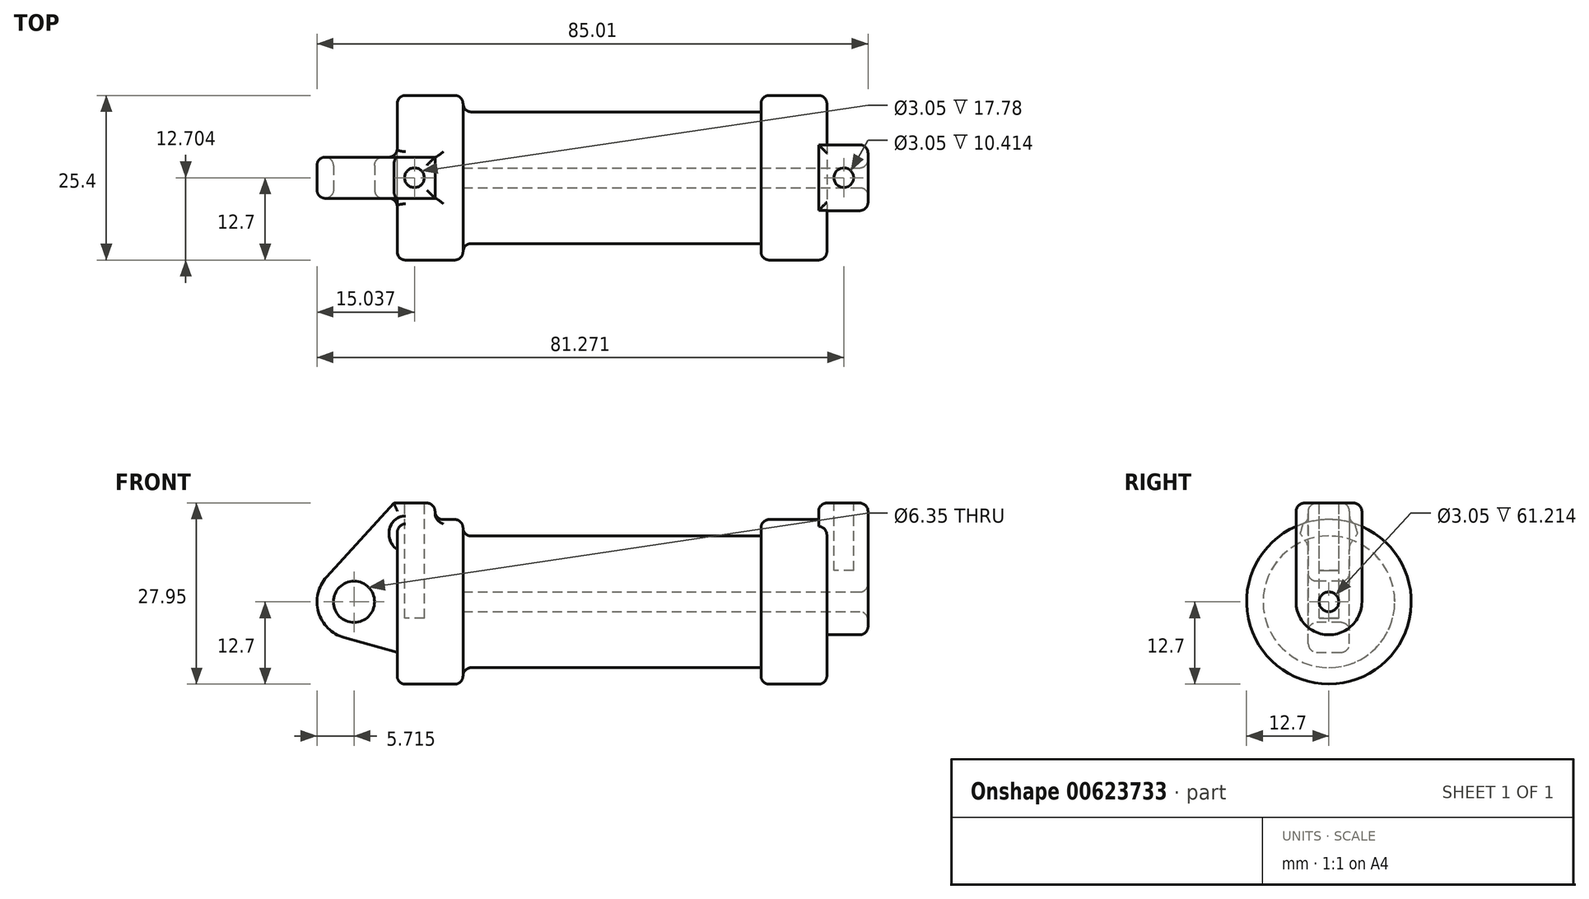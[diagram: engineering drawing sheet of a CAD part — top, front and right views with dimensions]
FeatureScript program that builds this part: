
annotation { "Feature Type Name" : "Feature", "Feature Type Description" : "" }
export const myFeature = defineFeature(function(context is Context, id is Id, definition is map)
    precondition{}
    {
        {
            var Q0;
            Q0=qCreatedBy(makeId("Front.planeOp"),FACE);
            var sketch = newSketch(context, id + "F0", { "sketchPlane" : qUnion([Q0])});
            skLineSegment(sketch, "E0", {"start": v(0, 0) * mm, "end": v(0, 12.7) * mm});
            skLineSegment(sketch, "E1", {"start": v(0, 12.7) * mm, "end": v(10.16, 12.7) * mm});
            skLineSegment(sketch, "E2", {"start": v(10.16, 12.7) * mm, "end": v(10.16, 10.16) * mm});
            skLineSegment(sketch, "E3", {"start": v(10.16, 10.16) * mm, "end": v(56.13, 10.16) * mm});
            skLineSegment(sketch, "E4", {"start": v(56.13, 10.16) * mm, "end": v(56.13, 12.7) * mm});
            skLineSegment(sketch, "E5", {"start": v(56.13, 12.7) * mm, "end": v(66.3, 12.7) * mm});
            skLineSegment(sketch, "E6", {"start": v(66.3, 12.7) * mm, "end": v(66.3, 0) * mm});
            skLineSegment(sketch, "E7", {"start": v(66.3, 0) * mm, "end": v(0, 0) * mm});
            skLineSegment(sketch, "E8", {"start": v(5.84, 15.24) * mm, "end": v(-0.5, 15.24) * mm});
            skLineSegment(sketch, "E9", {"start": v(-0.5, 15.24) * mm, "end": v(-10.88, 3.85) * mm});
            skLineSegment(sketch, "E10", {"start": v(0, 0) * mm, "end": v(-6.65, 0) * mm});
            skCircle(sketch, "E11", {"center": v(-6.65, 0) * mm, "radius": 5.72 * mm});
            skCircle(sketch, "E12", {"center": v(-6.65, 0) * mm, "radius": 3.18 * mm});
            skLineSegment(sketch, "E13", {"start": v(5.84, 15.24) * mm, "end": v(5.84, -9.4) * mm});
            skLineSegment(sketch, "E14", {"start": v(5.84, -9.4) * mm, "end": v(-8.18, -5.5) * mm});
            skSolve(sketch);
        }
        {
            var Q0;
            {var subQ0=sQuery(id+"F0.wireOp",EDGE,"E0");Q0=makeQuery(id+"F0.imprint","IMPRINT",FACE,{"disambiguationData":[TD([[makeQuery(id+"F0.imprint","IMPRINT",EDGE,{"derivedFrom":subQ0}),-1.0]])]});}
            var Q1;
            {var subQ1=sQuery(id+"F0.wireOp",EDGE,"E0");Q1=makeQuery(id+"F0.imprint","IMPRINT",FACE,{"disambiguationData":[TD([[makeQuery(id+"F0.imprint","IMPRINT",EDGE,{"derivedFrom":subQ1}),1.0]])]});}
            var Q2;
            {var subQ0=sQuery(id+"F0.wireOp",EDGE,"E14");Q2=makeQuery(id+"F0.imprint","IMPRINT",FACE,{"disambiguationData":[TD([[makeQuery(id+"F0.imprint","IMPRINT",EDGE,{"derivedFrom":subQ0}),-1.0]])]});}
            var Q3;
            {var subQ5=sQuery(id+"F0.wireOp",EDGE,"E12");Q3=makeQuery(id+"F0.imprint","IMPRINT",FACE,{"disambiguationData":[TD([[makeQuery(id+"F0.imprint","IMPRINT",EDGE,{"derivedFrom":subQ5}),-1.0]])]});}
            extrude(context, id + "F1", {"entities" : qUnion([Q0, Q1, Q2, Q3]), "endBound" : BoundingType.SYMMETRIC, "oppositeDirection" : true, "depth" : 6.35 * mm, "offsetDistance" : 25.4 * mm});
        }
        {
            var Q0;
            {var subQ0=sQuery(id+"F0.wireOp",EDGE,"E2");Q0=makeQuery(id+"F0.imprint","IMPRINT",FACE,{"disambiguationData":[TD([[makeQuery(id+"F0.imprint","IMPRINT",EDGE,{"derivedFrom":subQ0}),-1.0]])]});}
            var Q1;
            {var subQ0=sQuery(id+"F0.wireOp",EDGE,"E0");Q1=makeQuery(id+"F0.imprint","IMPRINT",FACE,{"disambiguationData":[TD([[makeQuery(id+"F0.imprint","IMPRINT",EDGE,{"derivedFrom":subQ0}),-1.0]])]});}
            var Q2;
            Q2=sQuery(id+"F0.wireOp",EDGE,"E7");
            revolve(context, id + "F2", {"operationType" : NewBodyOperationType.ADD, "entities" : qUnion([Q0, Q1]), "axis" : qUnion([Q2]), "revolveType" : RevolveType.FULL});
        }
        {
            var Q0;
            Q0=makeQuery(id+"F2.opRevolve","SWEPT_FACE",FACE,{"disambiguationData":[OSD([sQuery(id+"F0.wireOp",EDGE,"E6")])]});
            var sketch = newSketch(context, id + "F3", { "sketchPlane" : qUnion([Q0])});
            skCircle(sketch, "E15", {"center": v(0, 0) * mm, "radius": 5.08 * mm});
            skCircle(sketch, "E16", {"center": v(0, 0) * mm, "radius": 1.52 * mm});
            skLineSegment(sketch, "E17", {"start": v(5.08, 0) * mm, "end": v(5.08, 15.23) * mm});
            skLineSegment(sketch, "E18", {"start": v(-5.05, 15.25) * mm, "end": v(5.08, 15.23) * mm});
            skLineSegment(sketch, "E19", {"start": v(-5.05, 15.25) * mm, "end": v(-5.08, 0.01) * mm});
            skSolve(sketch);
        }
        {
            var Q0;
            {var subQ0=sQuery(id+"F3.wireOp",EDGE,"E18");Q0=makeQuery(id+"F3.imprint","IMPRINT",FACE,{"disambiguationData":[TD([[makeQuery(id+"F3.imprint","IMPRINT",EDGE,{"derivedFrom":subQ0}),-1.0]])]});}
            extrude(context, id + "F4", {"entities" : qUnion([Q0]), "operationType" : NewBodyOperationType.ADD, "oppositeDirection" : true, "depth" : 1.27 * mm, "offsetDistance" : 25.4 * mm});
        }
        {
            var Q0;
            Q0=makeQuery(id+"F3.imprint","IMPRINT",FACE,{"disambiguationData":[TD([[makeQuery(id+"F3.imprint","IMPRINT",EDGE,{"derivedFrom":sQuery(id+"F3.wireOp",EDGE,"E16")}),1.0]])]});
            var Q1;
            Q1=makeQuery(id+"F2.opRevolve","SWEPT_FACE",FACE,{"disambiguationData":[OSD([sQuery(id+"F0.wireOp",EDGE,"E2")])]});
            extrude(context, id + "F5", {"entities" : qUnion([Q0]), "operationType" : NewBodyOperationType.REMOVE, "endBound" : BoundingType.UP_TO_SURFACE, "oppositeDirection" : true, "depth" : 25.4 * mm, "endBoundEntityFace" : qUnion([Q1]), "offsetDistance" : 25.4 * mm});
        }
        {
            var Q0;
            Q0=makeQuery(id+"F3.imprint","IMPRINT",FACE,{"disambiguationData":[TD([[makeQuery(id+"F3.imprint","IMPRINT",EDGE,{"derivedFrom":sQuery(id+"F3.wireOp",EDGE,"E16")}),-1.0]])]});
            var Q1;
            {var subQ0=sQuery(id+"F3.wireOp",EDGE,"E17");var subQ1=sQuery(id+"F3.wireOp",EDGE,"E15");var subQ2=makeQuery(id+"F3.imprint","INTERSECT",VERTEX,{"derivedFrom":[subQ1,subQ0]});Q1=makeQuery(id+"F3.imprint","IMPRINT",FACE,{"disambiguationData":[TD([[makeQuery(id+"F3.imprint","IMPRINT",EDGE,{"disambiguationData":[TD([[subQ2,-1.0]])],"derivedFrom":subQ1}),-1.0]])]});}
            var Q2;
            {var subQ0=sQuery(id+"F3.wireOp",EDGE,"E18");Q2=makeQuery(id+"F3.imprint","IMPRINT",FACE,{"disambiguationData":[TD([[makeQuery(id+"F3.imprint","IMPRINT",EDGE,{"derivedFrom":subQ0}),-1.0]])]});}
            extrude(context, id + "F6", {"entities" : qUnion([Q0, Q1, Q2]), "operationType" : NewBodyOperationType.ADD, "depth" : 6.35 * mm, "offsetDistance" : 25.4 * mm});
        }
        {
            var Q0;
            Q0=makeQuery(id+"F1.opExtrude","SWEPT_FACE",FACE,{"disambiguationData":[OSD([sQuery(id+"F0.wireOp",EDGE,"E8")])]});
            var sketch = newSketch(context, id + "F7", { "sketchPlane" : qUnion([Q0])});
            skCircle(sketch, "E20", {"center": v(2.67, 0) * mm, "radius": 1.52 * mm});
            skPoint(sketch, "E20.centerSnap0", {"position": v(2.67, 3.18) * mm});
            skPoint(sketch, "E20.centerSnap1", {"position": v(5.84, 0) * mm});
            skCircle(sketch, "E21", {"center": v(68.9, 0) * mm, "radius": 1.52 * mm});
            skSolve(sketch);
        }
        {
            var Q0;
            Q0=makeQuery(id+"F7.imprint","IMPRINT",FACE,{"disambiguationData":[TD([[makeQuery(id+"F7.imprint","IMPRINT",EDGE,{"derivedFrom":sQuery(id+"F7.wireOp",EDGE,"E20")}),1.0]])]});
            extrude(context, id + "F8", {"entities" : qUnion([Q0]), "operationType" : NewBodyOperationType.REMOVE, "oppositeDirection" : true, "depth" : 17.78 * mm, "offsetDistance" : 25.4 * mm});
        }
        {
            var Q0;
            Q0=makeQuery(id+"F7.imprint","IMPRINT",FACE,{"disambiguationData":[TD([[makeQuery(id+"F7.imprint","IMPRINT",EDGE,{"derivedFrom":sQuery(id+"F7.wireOp",EDGE,"E21")}),1.0]])]});
            extrude(context, id + "F9", {"entities" : qUnion([Q0]), "operationType" : NewBodyOperationType.REMOVE, "oppositeDirection" : true, "depth" : 10.4 * mm, "offsetDistance" : 25.4 * mm});
        }
        {
            var Q0;
            Q0=makeQuery(id+"F2.opRevolve","SWEPT_EDGE",EDGE,{"disambiguationData":[OSD([sQuery(id+"F0.wireOp",EDGE,"E2"),sQuery(id+"F0.wireOp",EDGE,"E3")])]});
            var Q1;
            Q1=makeQuery(id+"F2.opRevolve","SWEPT_EDGE",EDGE,{"disambiguationData":[OSD([sQuery(id+"F0.wireOp",EDGE,"E1"),sQuery(id+"F0.wireOp",EDGE,"E2")])]});
            var Q2;
            Q2=makeQuery(id+"F2.boolean.opBoolean","INTERSECT",EDGE,{"derivedFrom":[makeQuery(id+"F1.opExtrude","CAP_FACE",FACE,{"disambiguationData":[OSD([sQuery(id+"F0.wireOp",EDGE,"E8"),sQuery(id+"F0.wireOp",EDGE,"E9"),sQuery(id+"F0.wireOp",EDGE,"E11"),sQuery(id+"F0.wireOp",EDGE,"E12"),sQuery(id+"F0.wireOp",EDGE,"E13"),sQuery(id+"F0.wireOp",EDGE,"E14")])],"isStart":true}),makeQuery(id+"F2.opRevolve","SWEPT_FACE",FACE,{"disambiguationData":[OSD([sQuery(id+"F0.wireOp",EDGE,"E1")])]})]});
            var Q3;
            Q3=makeQuery(id+"F2.boolean.opBoolean","INTERSECT",EDGE,{"derivedFrom":[makeQuery(id+"F1.opExtrude","SWEPT_FACE",FACE,{"disambiguationData":[OSD([sQuery(id+"F0.wireOp",EDGE,"E13")])]}),makeQuery(id+"F2.opRevolve","SWEPT_FACE",FACE,{"disambiguationData":[OSD([sQuery(id+"F0.wireOp",EDGE,"E1")])]})]});
            var Q4;
            Q4=makeQuery(id+"F2.boolean.opBoolean","INTERSECT",EDGE,{"derivedFrom":[makeQuery(id+"F1.opExtrude","CAP_FACE",FACE,{"disambiguationData":[OSD([sQuery(id+"F0.wireOp",EDGE,"E8"),sQuery(id+"F0.wireOp",EDGE,"E9"),sQuery(id+"F0.wireOp",EDGE,"E11"),sQuery(id+"F0.wireOp",EDGE,"E12"),sQuery(id+"F0.wireOp",EDGE,"E13"),sQuery(id+"F0.wireOp",EDGE,"E14")])],"isStart":false}),makeQuery(id+"F2.opRevolve","SWEPT_FACE",FACE,{"disambiguationData":[OSD([sQuery(id+"F0.wireOp",EDGE,"E1")])]})]});
            var Q5;
            Q5=makeQuery(id+"F1.opExtrude","CAP_EDGE",EDGE,{"disambiguationData":[OSD([sQuery(id+"F0.wireOp",EDGE,"E8")])],"isStart":false});
            var Q6;
            Q6=makeQuery(id+"F1.opExtrude","CAP_EDGE",EDGE,{"disambiguationData":[OSD([sQuery(id+"F0.wireOp",EDGE,"E8")])],"isStart":true});
            var Q7;
            Q7=makeQuery(id+"F1.opExtrude","SWEPT_EDGE",EDGE,{"disambiguationData":[OSD([sQuery(id+"F0.wireOp",EDGE,"E8"),sQuery(id+"F0.wireOp",EDGE,"E13")])]});
            var Q8;
            Q8=makeQuery(id+"F1.opExtrude","CAP_EDGE",EDGE,{"disambiguationData":[OSD([sQuery(id+"F0.wireOp",EDGE,"E9")])],"isStart":false});
            var Q9;
            Q9=makeQuery(id+"F1.opExtrude","CAP_EDGE",EDGE,{"disambiguationData":[OSD([sQuery(id+"F0.wireOp",EDGE,"E9")])],"isStart":true});
            var Q10;
            Q10=makeQuery(id+"F2.opRevolve","SWEPT_EDGE",EDGE,{"disambiguationData":[OSD([sQuery(id+"F0.wireOp",EDGE,"E0"),sQuery(id+"F0.wireOp",EDGE,"E1")])]});
            var Q11;
            Q11=makeQuery(id+"F1.opExtrude","CAP_EDGE",EDGE,{"disambiguationData":[OSD([sQuery(id+"F0.wireOp",EDGE,"E12")])],"isStart":false});
            var Q12;
            Q12=makeQuery(id+"F1.opExtrude","CAP_EDGE",EDGE,{"disambiguationData":[OSD([sQuery(id+"F0.wireOp",EDGE,"E12")])],"isStart":true});
            var Q13;
            Q13=makeQuery(id+"F8.boolean.opBoolean","COPY",EDGE,{"derivedFrom":makeQuery(id+"F8.opExtrude","CAP_EDGE",EDGE,{"disambiguationData":[OSD([sQuery(id+"F7.wireOp",EDGE,"E20")])],"isStart":true})});
            var Q14;
            Q14=makeQuery(id+"F2.opRevolve","SWEPT_EDGE",EDGE,{"disambiguationData":[OSD([sQuery(id+"F0.wireOp",EDGE,"E4"),sQuery(id+"F0.wireOp",EDGE,"E5")])]});
            var Q15;
            Q15=makeQuery(id+"F2.opRevolve","SWEPT_EDGE",EDGE,{"disambiguationData":[OSD([sQuery(id+"F0.wireOp",EDGE,"E5"),sQuery(id+"F0.wireOp",EDGE,"E6")])]});
            var Q16;
            Q16=makeQuery(id+"F6.opExtrude","CAP_EDGE",EDGE,{"disambiguationData":[OSD([sQuery(id+"F3.wireOp",EDGE,"E17")])],"isStart":true});
            var Q17;
            Q17=makeQuery(id+"F6.opExtrude","CAP_EDGE",EDGE,{"disambiguationData":[OSD([sQuery(id+"F3.wireOp",EDGE,"E15")])],"isStart":false});
            var Q18;
            Q18=makeQuery(id+"F6.opExtrude","CAP_EDGE",EDGE,{"disambiguationData":[OSD([sQuery(id+"F3.wireOp",EDGE,"E19")])],"isStart":false});
            var Q19;
            {var subQ0=sQuery(id+"F3.wireOp",EDGE,"E18");var subQ1=sQuery(id+"F3.wireOp",EDGE,"E17");Q19=makeQuery(id+"F6.boolean.opBoolean","MERGE",EDGE,{"derivedFrom":[makeQuery(id+"F4.opExtrude","SWEPT_EDGE",EDGE,{"disambiguationData":[OSD([subQ1,subQ0])]}),makeQuery(id+"F6.opExtrude","SWEPT_EDGE",EDGE,{"disambiguationData":[OSD([subQ1,subQ0])]})]});}
            var Q20;
            Q20=makeQuery(id+"F9.boolean.opBoolean","COPY",EDGE,{"derivedFrom":makeQuery(id+"F9.opExtrude","CAP_EDGE",EDGE,{"disambiguationData":[OSD([sQuery(id+"F7.wireOp",EDGE,"E21")])],"isStart":true})});
            var Q21;
            Q21=makeQuery(id+"F6.opExtrude","CAP_EDGE",EDGE,{"disambiguationData":[OSD([sQuery(id+"F3.wireOp",EDGE,"E18")])],"isStart":false});
            var Q22;
            Q22=makeQuery(id+"F4.opExtrude","CAP_EDGE",EDGE,{"disambiguationData":[OSD([sQuery(id+"F3.wireOp",EDGE,"E18")])],"isStart":false});
            var Q23;
            {var subQ0=sQuery(id+"F3.wireOp",EDGE,"E19");var subQ1=sQuery(id+"F3.wireOp",EDGE,"E18");Q23=makeQuery(id+"F6.boolean.opBoolean","MERGE",EDGE,{"derivedFrom":[makeQuery(id+"F4.opExtrude","SWEPT_EDGE",EDGE,{"disambiguationData":[OSD([subQ1,subQ0])]}),makeQuery(id+"F6.opExtrude","SWEPT_EDGE",EDGE,{"disambiguationData":[OSD([subQ1,subQ0])]})]});}
            var Q24;
            Q24=makeQuery(id+"F6.opExtrude","CAP_EDGE",EDGE,{"disambiguationData":[OSD([sQuery(id+"F3.wireOp",EDGE,"E16")])],"isStart":false});
            fillet(context, id + "F10", {"entities" : qUnion([Q0, Q1, Q2, Q3, Q4, Q5, Q6, Q7, Q8, Q9, Q10, Q11, Q12, Q13, Q14, Q15, Q16, Q17, Q18, Q19, Q20, Q21, Q22, Q23, Q24]), "radius" : 1.27 * mm, "tangentPropagation" : true, "allowEdgeOverflow" : false});
        }
    });
